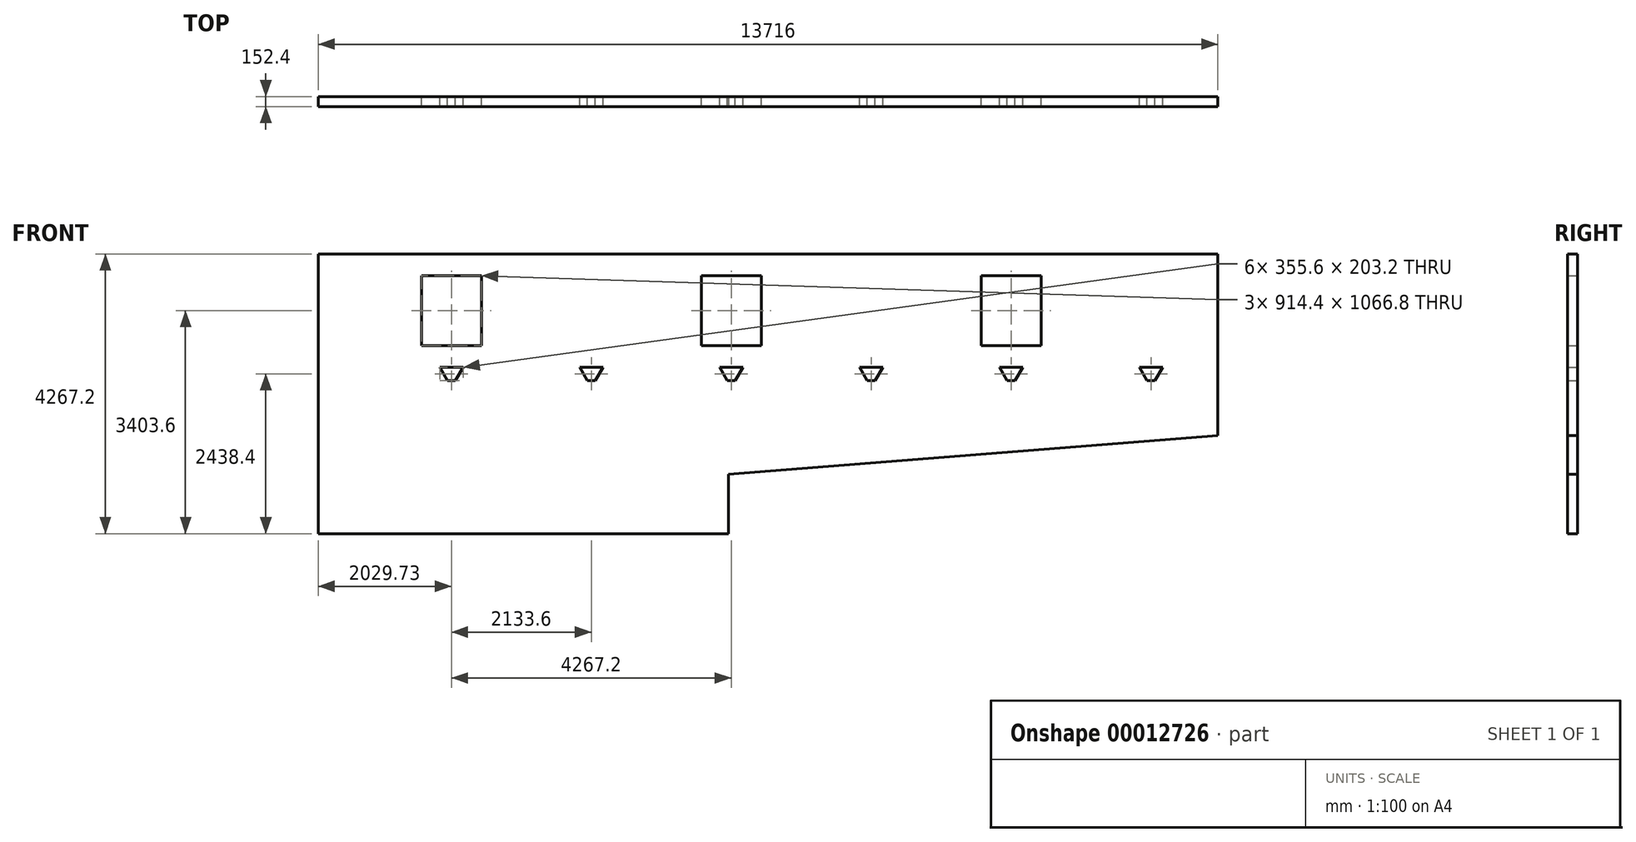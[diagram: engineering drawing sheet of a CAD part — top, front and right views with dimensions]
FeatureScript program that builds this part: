
annotation { "Feature Type Name" : "Feature", "Feature Type Description" : "" }
export const myFeature = defineFeature(function(context is Context, id is Id, definition is map)
    precondition{}
    {
        {
            var Q0;
            Q0=qCreatedBy(makeId("Front.planeOp"),FACE);
            var sketch = newSketch(context, id + "F0", { "sketchPlane" : qUnion([Q0])});
            skLineSegment(sketch, "E0.bottom", {"start": v(-13716, 4267.2) * mm, "end": v(0, 4267.2) * mm});
            skLineSegment(sketch, "E0.top", {"start": v(-13716, 0) * mm, "end": v(0, 0) * mm});
            skLineSegment(sketch, "E0.left", {"start": v(-13716, 4267.2) * mm, "end": v(-13716, 0) * mm});
            skLineSegment(sketch, "E0.right", {"start": v(0, 4267.2) * mm, "end": v(0, 0) * mm});
            skLineSegment(sketch, "E1.bottom", {"start": v(-12143.47, 3937) * mm, "end": v(-11229.07, 3937) * mm});
            skLineSegment(sketch, "E1.top", {"start": v(-12143.47, 2870.2) * mm, "end": v(-11229.07, 2870.2) * mm});
            skLineSegment(sketch, "E1.left", {"start": v(-12143.47, 3937) * mm, "end": v(-12143.47, 2870.2) * mm});
            skLineSegment(sketch, "E1.right", {"start": v(-11229.07, 3937) * mm, "end": v(-11229.07, 2870.2) * mm});
            skLineSegment(sketch, "E2.1.0.0", {"start": v(-7876.27, 3937) * mm, "end": v(-6961.87, 3937) * mm});
            skLineSegment(sketch, "E2.1.0.1", {"start": v(-7876.27, 3937) * mm, "end": v(-7876.27, 2870.2) * mm});
            skLineSegment(sketch, "E2.1.0.2", {"start": v(-7876.27, 2870.2) * mm, "end": v(-6961.87, 2870.2) * mm});
            skLineSegment(sketch, "E2.1.0.3", {"start": v(-6961.87, 3937) * mm, "end": v(-6961.87, 2870.2) * mm});
            skLineSegment(sketch, "E2.2.0.0", {"start": v(-3609.07, 3937) * mm, "end": v(-2694.67, 3937) * mm});
            skLineSegment(sketch, "E2.2.0.1", {"start": v(-3609.07, 3937) * mm, "end": v(-3609.07, 2870.2) * mm});
            skLineSegment(sketch, "E2.2.0.2", {"start": v(-3609.07, 2870.2) * mm, "end": v(-2694.67, 2870.2) * mm});
            skLineSegment(sketch, "E2.2.0.3", {"start": v(-2694.67, 3937) * mm, "end": v(-2694.67, 2870.2) * mm});
            skLineSegment(sketch, "E2.direction1", {"start": v(-12143.47, 3937) * mm, "end": v(-7876.27, 3937) * mm, "construction": true});
            skLineSegment(sketch, "E3", {"start": v(-11864.07, 2540) * mm, "end": v(-11746.75, 2336.8) * mm});
            skLineSegment(sketch, "E4", {"start": v(-11746.75, 2336.8) * mm, "end": v(-11625.79, 2336.8) * mm});
            skLineSegment(sketch, "E5", {"start": v(-11625.79, 2336.8) * mm, "end": v(-11508.47, 2540) * mm});
            skLineSegment(sketch, "E6", {"start": v(-11508.47, 2540) * mm, "end": v(-11864.07, 2540) * mm});
            skLineSegment(sketch, "E7", {"start": v(-11229.07, 2870.2) * mm, "end": v(-7876.27, 2870.2) * mm, "construction": true});
            skLineSegment(sketch, "E8.1.0.0", {"start": v(-9374.87, 2540) * mm, "end": v(-9730.47, 2540) * mm});
            skLineSegment(sketch, "E8.1.0.1", {"start": v(-9730.47, 2540) * mm, "end": v(-9613.15, 2336.8) * mm});
            skLineSegment(sketch, "E8.1.0.2", {"start": v(-9492.19, 2336.8) * mm, "end": v(-9374.87, 2540) * mm});
            skLineSegment(sketch, "E8.1.0.3", {"start": v(-9613.15, 2336.8) * mm, "end": v(-9492.19, 2336.8) * mm});
            skLineSegment(sketch, "E8.2.0.0", {"start": v(-7241.27, 2540) * mm, "end": v(-7596.87, 2540) * mm});
            skLineSegment(sketch, "E8.2.0.1", {"start": v(-7596.87, 2540) * mm, "end": v(-7479.55, 2336.8) * mm});
            skLineSegment(sketch, "E8.2.0.2", {"start": v(-7358.59, 2336.8) * mm, "end": v(-7241.27, 2540) * mm});
            skLineSegment(sketch, "E8.2.0.3", {"start": v(-7479.55, 2336.8) * mm, "end": v(-7358.59, 2336.8) * mm});
            skLineSegment(sketch, "E8.3.0.0", {"start": v(-5107.67, 2540) * mm, "end": v(-5463.27, 2540) * mm});
            skLineSegment(sketch, "E8.3.0.1", {"start": v(-5463.27, 2540) * mm, "end": v(-5345.95, 2336.8) * mm});
            skLineSegment(sketch, "E8.3.0.2", {"start": v(-5224.99, 2336.8) * mm, "end": v(-5107.67, 2540) * mm});
            skLineSegment(sketch, "E8.3.0.3", {"start": v(-5345.95, 2336.8) * mm, "end": v(-5224.99, 2336.8) * mm});
            skLineSegment(sketch, "E8.4.0.0", {"start": v(-2974.07, 2540) * mm, "end": v(-3329.67, 2540) * mm});
            skLineSegment(sketch, "E8.4.0.1", {"start": v(-3329.67, 2540) * mm, "end": v(-3212.35, 2336.8) * mm});
            skLineSegment(sketch, "E8.4.0.2", {"start": v(-3091.39, 2336.8) * mm, "end": v(-2974.07, 2540) * mm});
            skLineSegment(sketch, "E8.4.0.3", {"start": v(-3212.35, 2336.8) * mm, "end": v(-3091.39, 2336.8) * mm});
            skLineSegment(sketch, "E8.5.0.0", {"start": v(-840.47, 2540) * mm, "end": v(-1196.07, 2540) * mm});
            skLineSegment(sketch, "E8.5.0.1", {"start": v(-1196.07, 2540) * mm, "end": v(-1078.75, 2336.8) * mm});
            skLineSegment(sketch, "E8.5.0.2", {"start": v(-957.79, 2336.8) * mm, "end": v(-840.47, 2540) * mm});
            skLineSegment(sketch, "E8.5.0.3", {"start": v(-1078.75, 2336.8) * mm, "end": v(-957.79, 2336.8) * mm});
            skLineSegment(sketch, "E8.direction1", {"start": v(-11864.07, 2540) * mm, "end": v(-9730.47, 2540) * mm, "construction": true});
            skPoint(sketch, "E9", {"position": v(-11686.27, 2540) * mm});
            skPoint(sketch, "E10", {"position": v(-11686.27, 2870.2) * mm});
            skSolve(sketch);
        }
        {
            var Q0;
            Q0=makeQuery(id+"F0.imprint","IMPRINT",FACE,{"disambiguationData":[TD([[makeQuery(id+"F0.imprint","IMPRINT",EDGE,{"derivedFrom":sQuery(id+"F0.wireOp",EDGE,"E0.bottom")}),-1.0]])]});
            extrude(context, id + "F1", {"entities" : qUnion([Q0]), "depth" : 152.4 * mm});
        }
        {
            var Q0;
            Q0=makeQuery(id+"F1.opExtrude","CAP_FACE",FACE,{"disambiguationData":[OSD([sQuery(id+"F0.wireOp",EDGE,"E0.bottom"),sQuery(id+"F0.wireOp",EDGE,"E0.top"),sQuery(id+"F0.wireOp",EDGE,"E0.left"),sQuery(id+"F0.wireOp",EDGE,"E0.right"),sQuery(id+"F0.wireOp",EDGE,"E1.bottom"),sQuery(id+"F0.wireOp",EDGE,"E1.top"),sQuery(id+"F0.wireOp",EDGE,"E1.left"),sQuery(id+"F0.wireOp",EDGE,"E1.right"),sQuery(id+"F0.wireOp",EDGE,"E2.1.0.0"),sQuery(id+"F0.wireOp",EDGE,"E2.1.0.1"),sQuery(id+"F0.wireOp",EDGE,"E2.1.0.2"),sQuery(id+"F0.wireOp",EDGE,"E2.1.0.3"),sQuery(id+"F0.wireOp",EDGE,"E2.2.0.0"),sQuery(id+"F0.wireOp",EDGE,"E2.2.0.1"),sQuery(id+"F0.wireOp",EDGE,"E2.2.0.2"),sQuery(id+"F0.wireOp",EDGE,"E2.2.0.3"),sQuery(id+"F0.wireOp",EDGE,"E3"),sQuery(id+"F0.wireOp",EDGE,"E4"),sQuery(id+"F0.wireOp",EDGE,"E5"),sQuery(id+"F0.wireOp",EDGE,"E6"),sQuery(id+"F0.wireOp",EDGE,"E8.1.0.0"),sQuery(id+"F0.wireOp",EDGE,"E8.1.0.1"),sQuery(id+"F0.wireOp",EDGE,"E8.1.0.2"),sQuery(id+"F0.wireOp",EDGE,"E8.1.0.3"),sQuery(id+"F0.wireOp",EDGE,"E8.2.0.0"),sQuery(id+"F0.wireOp",EDGE,"E8.2.0.1"),sQuery(id+"F0.wireOp",EDGE,"E8.2.0.2"),sQuery(id+"F0.wireOp",EDGE,"E8.2.0.3"),sQuery(id+"F0.wireOp",EDGE,"E8.3.0.0"),sQuery(id+"F0.wireOp",EDGE,"E8.3.0.1"),sQuery(id+"F0.wireOp",EDGE,"E8.3.0.2"),sQuery(id+"F0.wireOp",EDGE,"E8.3.0.3"),sQuery(id+"F0.wireOp",EDGE,"E8.4.0.0"),sQuery(id+"F0.wireOp",EDGE,"E8.4.0.1"),sQuery(id+"F0.wireOp",EDGE,"E8.4.0.2"),sQuery(id+"F0.wireOp",EDGE,"E8.4.0.3"),sQuery(id+"F0.wireOp",EDGE,"E8.5.0.0"),sQuery(id+"F0.wireOp",EDGE,"E8.5.0.1"),sQuery(id+"F0.wireOp",EDGE,"E8.5.0.2"),sQuery(id+"F0.wireOp",EDGE,"E8.5.0.3")])],"isStart":false});
            var sketch = newSketch(context, id + "F2", { "sketchPlane" : qUnion([Q0])});
            skLineSegment(sketch, "E11", {"start": v(-7459.04, 904.88) * mm, "end": v(0, 1497.33) * mm});
            skLineSegment(sketch, "E12", {"start": v(-13716, 2019.3) * mm, "end": v(0, 2019.3) * mm, "construction": true});
            skLineSegment(sketch, "E13", {"start": v(-7419.07, 2336.8) * mm, "end": v(-7419.07, 908.05) * mm, "construction": true});
            skLineSegment(sketch, "E14", {"start": v(-7459.04, 904.88) * mm, "end": v(-7459.04, 0) * mm});
            skLineSegment(sketch, "E15", {"start": v(-7459.04, 0) * mm, "end": v(-5020.64, 0) * mm, "construction": true});
            skLineSegment(sketch, "E16", {"start": v(-5020.64, 0) * mm, "end": v(-5020.64, 1098.55) * mm, "construction": true});
            skLineSegment(sketch, "E17", {"start": v(-3151.87, 2336.8) * mm, "end": v(-3151.87, 1246.98) * mm, "construction": true});
            skSolve(sketch);
        }
        {
            var Q0;
            {var subQ4=sQuery(id+"F2.wireOp",EDGE,"E11");Q0=makeQuery(id+"F2.imprint","IMPRINT",FACE,{"disambiguationData":[TD([[makeQuery(id+"F2.imprint","IMPRINT",EDGE,{"derivedFrom":subQ4}),-1.0]])]});}
            extrude(context, id + "F3", {"entities" : qUnion([Q0]), "operationType" : NewBodyOperationType.REMOVE, "endBound" : BoundingType.THROUGH_ALL, "oppositeDirection" : true, "depth" : 25.4 * mm});
        }
    });
